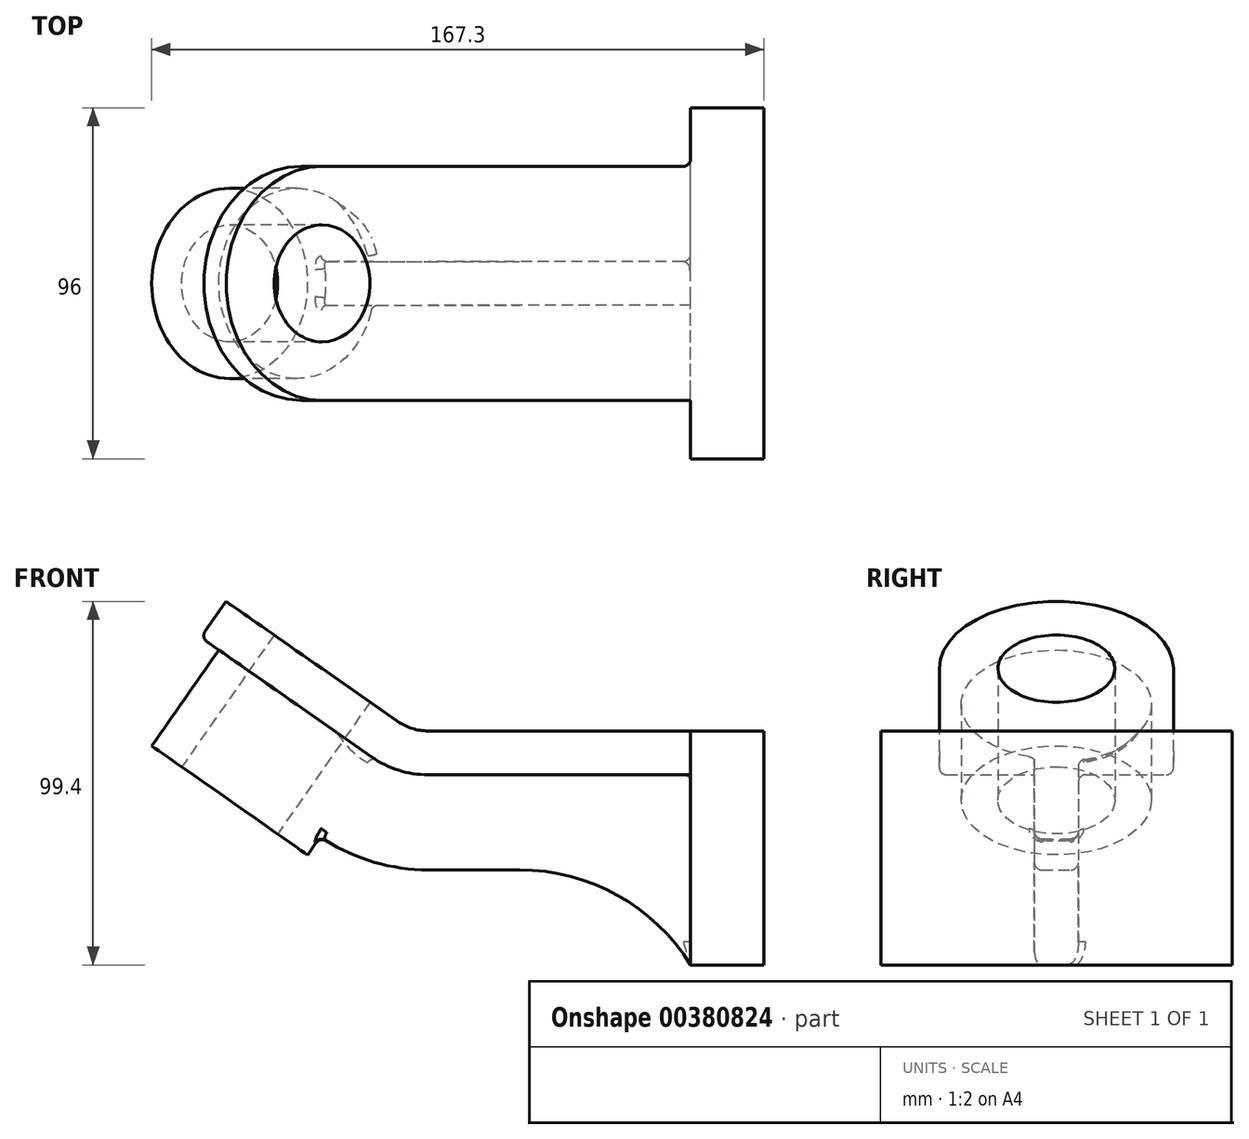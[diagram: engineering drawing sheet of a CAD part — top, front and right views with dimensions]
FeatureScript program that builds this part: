
annotation { "Feature Type Name" : "Feature", "Feature Type Description" : "" }
export const myFeature = defineFeature(function(context is Context, id is Id, definition is map)
    precondition{}
    {
        {
            var Q0;
            Q0=qCreatedBy(makeId("Right.planeOp"),FACE);
            var sketch = newSketch(context, id + "F0", { "sketchPlane" : qUnion([Q0])});
            skLineSegment(sketch, "E0.bottom", {"start": v(-48, 32) * mm, "end": v(48, 32) * mm});
            skLineSegment(sketch, "E0.top", {"start": v(-48, -32) * mm, "end": v(48, -32) * mm});
            skLineSegment(sketch, "E0.left", {"start": v(-48, 32) * mm, "end": v(-48, -32) * mm});
            skLineSegment(sketch, "E0.right", {"start": v(48, 32) * mm, "end": v(48, -32) * mm});
            skPoint(sketch, "E0.middle", {"position": v(0, 0) * mm});
            skSolve(sketch);
        }
        {
            var Q0;
            Q0=qSketchRegion(id+"F0",true);
            extrude(context, id + "F1", {"entities" : qUnion([Q0]), "oppositeDirection" : true, "depth" : 20 * mm});
        }
        {
            var Q0;
            Q0=qCreatedBy(makeId("Front.planeOp"),FACE);
            var sketch = newSketch(context, id + "F2", { "sketchPlane" : qUnion([Q0])});
            skLineSegment(sketch, "E1", {"start": v(-20, 32) * mm, "end": v(-91.7, 32) * mm});
            skLineSegment(sketch, "E2", {"start": v(-100.3, 34.71) * mm, "end": v(-146.98, 67.4) * mm});
            skLineSegment(sketch, "E3", {"start": v(-120.76, 49.04) * mm, "end": v(-146, 13) * mm, "construction": true});
            skPoint(sketch, "E4.visualSharp", {"position": v(-96.42, 32) * mm});
            skArc(sketch, "E4.filletArc", {"start": v(-100.3, 34.71) * mm, "mid": v(-96.2, 32.7) * mm, "end": v(-91.7, 32) * mm});
            skLineSegment(sketch, "E5.0", {"start": v(-20, 20) * mm, "end": v(-91.7, 20) * mm});
            skArc(sketch, "E5.1", {"start": v(-107.18, 24.88) * mm, "mid": v(-99.81, 21.25) * mm, "end": v(-91.7, 20) * mm});
            skLineSegment(sketch, "E5.2", {"start": v(-107.18, 24.88) * mm, "end": v(-153.86, 57.57) * mm});
            skLineSegment(sketch, "E6", {"start": v(-153.86, 57.57) * mm, "end": v(-146.98, 67.4) * mm});
            skLineSegment(sketch, "E7", {"start": v(-20, 20) * mm, "end": v(-20, 32) * mm});
            skSolve(sketch);
        }
        {
            var Q0;
            Q0=qSketchRegion(id+"F2",true);
            extrude(context, id + "F3", {"entities" : qUnion([Q0]), "operationType" : NewBodyOperationType.ADD, "endBound" : BoundingType.SYMMETRIC, "depth" : 64 * mm});
        }
        {
            var Q0;
            Q0=sQuery(id+"F2.wireOp",VERTEX,"E3.end");
            var Q1;
            Q1=sQuery(id+"F2.wireOp",EDGE,"E3");
            cPlane(context, id + "F4", {"entities" : qUnion([Q0, Q1]), "cplaneType" : CPlaneType.LINE_POINT, "offset" : 25 * mm, "width" : 150 * mm, "height" : 150 * mm});
        }
        {
            var Q0;
            Q0=makeQuery(id+"F3.opExtrude","CAP_EDGE",EDGE,{"disambiguationData":[OSD([sQuery(id+"F2.wireOp",EDGE,"E6")])],"isStart":false});
            var Q1;
            Q1=makeQuery(id+"F3.opExtrude","CAP_EDGE",EDGE,{"disambiguationData":[OSD([sQuery(id+"F2.wireOp",EDGE,"E6")])],"isStart":true});
            fillet(context, id + "F5", {"entities" : qUnion([Q0, Q1]), "radius" : 32 * mm, "tangentPropagation" : true, "allowEdgeOverflow" : false});
        }
        {
            var Q0;
            Q0=qCreatedBy(id+"F4.planeOp",FACE);
            var sketch = newSketch(context, id + "F6", { "sketchPlane" : qUnion([Q0])});
            skCircle(sketch, "E8", {"center": v(-127.05, 0) * mm, "radius": 26 * mm});
            skSolve(sketch);
        }
        {
            var Q0;
            Q0=qSketchRegion(id+"F6",true);
            extrude(context, id + "F7", {"entities" : qUnion([Q0]), "operationType" : NewBodyOperationType.ADD, "endBound" : BoundingType.UP_TO_NEXT, "oppositeDirection" : true, "depth" : 25 * mm});
        }
        {
            var Q0;
            Q0=makeQuery(id+"F7.opExtrude","CAP_FACE",FACE,{"disambiguationData":[OSD([sQuery(id+"F6.wireOp",EDGE,"E8")])],"isStart":true});
            var sketch = newSketch(context, id + "F8", { "sketchPlane" : qUnion([Q0])});
            skCircle(sketch, "E9", {"center": v(-127.05, 0) * mm, "radius": 16 * mm});
            skSolve(sketch);
        }
        {
            var Q0;
            Q0=qCreatedBy(makeId("Front.planeOp"),FACE);
            var sketch = newSketch(context, id + "F9", { "sketchPlane" : qUnion([Q0])});
            skLineSegment(sketch, "E10.0", {"start": v(-122.1, 3.58) * mm, "end": v(-142.56, 17.91) * mm});
            skArc(sketch, "E10.1", {"start": v(-122.1, 3.58) * mm, "mid": v(-107.63, -3.55) * mm, "end": v(-91.7, -6) * mm});
            skArc(sketch, "E11", {"start": v(-66.73, -6) * mm, "mid": v(-40, -12.94) * mm, "end": v(-20, -32) * mm});
            skLineSegment(sketch, "E12.0", {"start": v(-20, 20) * mm, "end": v(-91.7, 20) * mm});
            skArc(sketch, "E13.0", {"start": v(-107.18, 24.88) * mm, "mid": v(-99.81, 21.25) * mm, "end": v(-91.7, 20) * mm});
            skLineSegment(sketch, "E14.0", {"start": v(-107.18, 24.88) * mm, "end": v(-127.65, 39.21) * mm});
            skLineSegment(sketch, "E15.0", {"start": v(-127.65, 39.21) * mm, "end": v(-142.56, 17.91) * mm});
            skPoint(sketch, "E16.orphan", {"position": v(-146, 13) * mm});
            skPoint(sketch, "E17.orphan", {"position": v(-120.76, 49.04) * mm});
            skLineSegment(sketch, "E18.0", {"start": v(-20, 20) * mm, "end": v(-20, -32) * mm});
            skPoint(sketch, "E19.orphan", {"position": v(-20, 32) * mm});
            skLineSegment(sketch, "E20", {"start": v(-91.7, -6) * mm, "end": v(-66.73, -6) * mm});
            skSolve(sketch);
        }
        {
            var Q0;
            Q0=qSketchRegion(id+"F9",true);
            extrude(context, id + "F10", {"entities" : qUnion([Q0]), "operationType" : NewBodyOperationType.ADD, "endBound" : BoundingType.SYMMETRIC, "depth" : 12 * mm});
        }
        {
            var Q0;
            Q0=qSketchRegion(id+"F8",true);
            extrude(context, id + "F11", {"entities" : qUnion([Q0]), "operationType" : NewBodyOperationType.REMOVE, "endBound" : BoundingType.THROUGH_ALL, "oppositeDirection" : true, "depth" : 25 * mm});
        }
        {
            var Q0;
            Q0=makeQuery(id+"F3.opExtrude","CAP_EDGE",EDGE,{"disambiguationData":[OSD([sQuery(id+"F2.wireOp",EDGE,"E5.0")])],"isStart":false});
            var Q1;
            Q1=makeQuery(id+"F10.opExtrude","CAP_EDGE",EDGE,{"disambiguationData":[OSD([sQuery(id+"F9.wireOp",EDGE,"E11")])],"isStart":false});
            var Q2;
            Q2=makeQuery(id+"F10.opExtrude","CAP_EDGE",EDGE,{"disambiguationData":[OSD([sQuery(id+"F9.wireOp",EDGE,"E11")])],"isStart":true});
            var Q3;
            Q3=makeQuery(id+"F10.opExtrude","CAP_EDGE",EDGE,{"disambiguationData":[OSD([sQuery(id+"F9.wireOp",EDGE,"E12.0")])],"isStart":false});
            var Q4;
            Q4=makeQuery(id+"F10.opExtrude","CAP_EDGE",EDGE,{"disambiguationData":[OSD([sQuery(id+"F9.wireOp",EDGE,"E12.0")])],"isStart":true});
            fillet(context, id + "F12", {"entities" : qUnion([Q0, Q1, Q2, Q3, Q4]), "radius" : 2 * mm, "tangentPropagation" : true, "allowEdgeOverflow" : false});
        }
        {
            var Q0;
            Q0=makeQuery(id+"F10.boolean.opBoolean","INTERSECT",EDGE,{"derivedFrom":[makeQuery(id+"F7.opExtrude","SWEPT_FACE",FACE,{"disambiguationData":[OSD([sQuery(id+"F6.wireOp",EDGE,"E8")])]}),makeQuery(id+"F10.opExtrude","CAP_FACE",FACE,{"disambiguationData":[OSD([sQuery(id+"F9.wireOp",EDGE,"E10.0"),sQuery(id+"F9.wireOp",EDGE,"E10.1"),sQuery(id+"F9.wireOp",EDGE,"E11"),sQuery(id+"F9.wireOp",EDGE,"E12.0"),sQuery(id+"F9.wireOp",EDGE,"E13.0"),sQuery(id+"F9.wireOp",EDGE,"E14.0"),sQuery(id+"F9.wireOp",EDGE,"E15.0"),sQuery(id+"F9.wireOp",EDGE,"E18.0")])],"isStart":false})]});
            var Q1;
            Q1=makeQuery(id+"F10.opExtrude","CAP_EDGE",EDGE,{"disambiguationData":[OSD([sQuery(id+"F9.wireOp",EDGE,"E18.0")])],"isStart":false});
            var Q2;
            Q2=makeQuery(id+"F10.opExtrude","CAP_EDGE",EDGE,{"disambiguationData":[OSD([sQuery(id+"F9.wireOp",EDGE,"E18.0")])],"isStart":true});
            fillet(context, id + "F13", {"entities" : qUnion([Q0, Q1, Q2]), "radius" : 2 * mm, "tangentPropagation" : true, "allowEdgeOverflow" : false});
        }
    });
